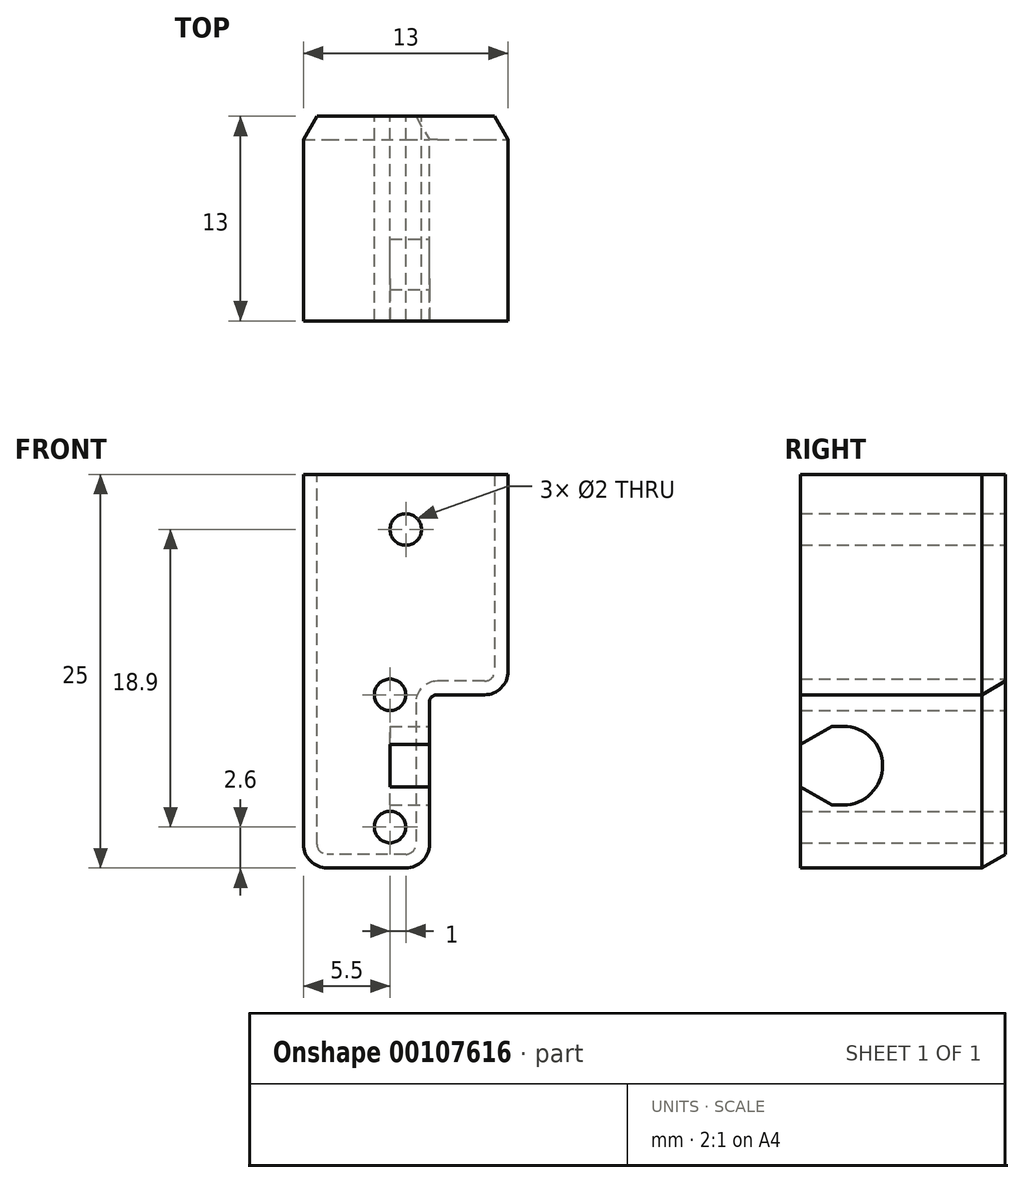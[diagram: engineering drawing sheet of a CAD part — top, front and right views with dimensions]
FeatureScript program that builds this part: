
annotation { "Feature Type Name" : "Feature", "Feature Type Description" : "" }
export const myFeature = defineFeature(function(context is Context, id is Id, definition is map)
    precondition{}
    {
        {
            var Q0;
            Q0=qCreatedBy(makeId("Front.planeOp"),FACE);
            var sketch = newSketch(context, id + "F0", { "sketchPlane" : qUnion([Q0])});
            skLineSegment(sketch, "E0", {"start": v(0, 0) * mm, "end": v(0, 25) * mm});
            skLineSegment(sketch, "E1", {"start": v(0, 25) * mm, "end": v(13, 25) * mm});
            skLineSegment(sketch, "E2", {"start": v(13, 25) * mm, "end": v(13, 11) * mm});
            skLineSegment(sketch, "E3", {"start": v(8, 0) * mm, "end": v(0, 0) * mm});
            skLineSegment(sketch, "E4", {"start": v(8, 0) * mm, "end": v(8, 11) * mm});
            skLineSegment(sketch, "E5", {"start": v(8, 11) * mm, "end": v(13, 11) * mm});
            skCircle(sketch, "E6", {"center": v(6.5, 21.5) * mm, "radius": 1 * mm});
            skCircle(sketch, "E7", {"center": v(5.5, 2.6) * mm, "radius": 1 * mm});
            skCircle(sketch, "E8", {"center": v(5.5, 11) * mm, "radius": 1 * mm});
            skSolve(sketch);
        }
        {
            var Q0;
            Q0 = qSketchRegion(id + "F0", true);
            extrude(context, id + "F1", {"entities" : qUnion([Q0]), "depth" : 13 * mm});
        }
        {
            var Q0;
            Q0=makeQuery(id+"F1.opExtrude","SWEPT_FACE",FACE,{"disambiguationData":[OSD([sQuery(id+"F0.wireOp",EDGE,"E4")])]});
            var sketch = newSketch(context, id + "F2", { "sketchPlane" : qUnion([Q0])});
            skLineSegment(sketch, "E9", {"start": v(-11, 4) * mm, "end": v(-10.3, 4) * mm});
            skLineSegment(sketch, "E10", {"start": v(-10.3, 9) * mm, "end": v(-11, 9) * mm});
            skArc(sketch, "E11", {"start": v(-10.3, 9) * mm, "mid": v(-7.8, 6.5) * mm, "end": v(-10.3, 4) * mm});
            skArc(sketch, "E12", {"start": v(-10.3, 9) * mm, "mid": v(-12.8, 6.5) * mm, "end": v(-10.3, 4) * mm, "construction": true});
            skLineSegment(sketch, "E13", {"start": v(-11, 9) * mm, "end": v(-13, 7.85) * mm});
            skLineSegment(sketch, "E14", {"start": v(-11, 4) * mm, "end": v(-13, 5.15) * mm});
            skLineSegment(sketch, "E15", {"start": v(-11, 9) * mm, "end": v(-11, 4) * mm, "construction": true});
            skLineSegment(sketch, "E16", {"start": v(-13, 7.85) * mm, "end": v(-13, 5.15) * mm});
            skSolve(sketch);
        }
        {
            var Q0;
            Q0 = qSketchRegion(id + "F2", true);
            extrude(context, id + "F3", {"entities" : qUnion([Q0]), "operationType" : NewBodyOperationType.REMOVE, "oppositeDirection" : true, "depth" : 2.5 * mm});
        }
        {
            var Q0;
            Q0=makeQuery(id+"F1.opExtrude","SWEPT_EDGE",EDGE,{"disambiguationData":[OSD([sQuery(id+"F0.wireOp",EDGE,"E3"),sQuery(id+"F0.wireOp",EDGE,"E4")])]});
            var Q1;
            Q1=makeQuery(id+"F1.opExtrude","SWEPT_EDGE",EDGE,{"disambiguationData":[OSD([sQuery(id+"F0.wireOp",EDGE,"E0"),sQuery(id+"F0.wireOp",EDGE,"E3")])]});
            var Q2;
            Q2=makeQuery(id+"F1.opExtrude","SWEPT_EDGE",EDGE,{"disambiguationData":[OSD([sQuery(id+"F0.wireOp",EDGE,"E2"),sQuery(id+"F0.wireOp",EDGE,"E5")])]});
            fillet(context, id + "F4", {"entities" : qUnion([Q0, Q1, Q2]), "radius" : 1.5 * mm, "tangentPropagation" : true, "allowEdgeOverflow" : false});
        }
        {
            var Q0;
            Q0=makeQuery(id+"F1.opExtrude","SWEPT_EDGE",EDGE,{"disambiguationData":[OSD([sQuery(id+"F0.wireOp",EDGE,"E4"),sQuery(id+"F0.wireOp",EDGE,"E5")])]});
            fillet(context, id + "F5", {"entities" : qUnion([Q0]), "radius" : 0.5 * mm, "tangentPropagation" : true, "allowEdgeOverflow" : false});
        }
        {
            var Q0;
            Q0=makeQuery(id+"F1.opExtrude","CAP_EDGE",EDGE,{"disambiguationData":[OSD([sQuery(id+"F0.wireOp",EDGE,"E2")])],"isStart":true});
            chamfer(context, id + "F6", {"entities" : qUnion([Q0]), "chamferType" : ChamferType.OFFSET_ANGLE, "width" : 1.5 * mm, "oppositeDirection" : true, "angle" : 30 * degree, "tangentPropagation" : true});
        }
    });
